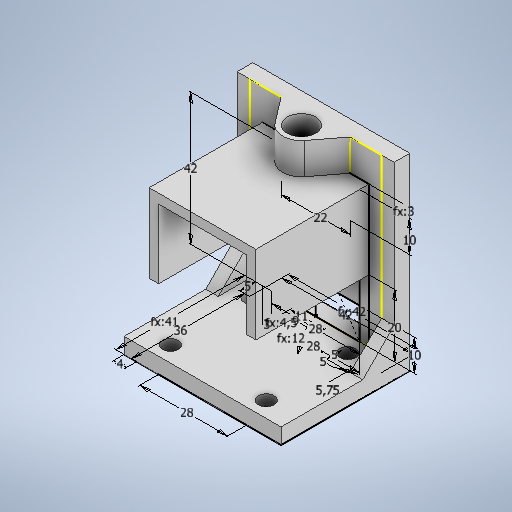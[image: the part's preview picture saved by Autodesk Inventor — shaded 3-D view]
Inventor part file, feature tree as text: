
AUTODESK INVENTOR PART (.ipt)
format: ipt  version: 2025 (Build 290162000, 162)  size: 386,560 bytes
history: native  units: mm
features: extrude x10, thread x4, sketch x2, chamfer x2, other x1, projected_geometry x1
ambient origin geometry x8: Origin, YZ Plane, XZ Plane, XY Plane, X Axis, Y Axis, Z Axis, Center Point
bodies: Body1 (feature_tree)
feature tree (20):
  other  "Bryła1"
  sketch  "Szkic1"
  extrude  "Wyciągnięcie proste1"  Depth=5.0mm
  extrude  "Wyciągnięcie proste2"  Depth=5.75mm
  extrude  "Wyciągnięcie proste3"  Depth=5.0mm
  extrude  "Wyciągnięcie proste4"  Depth=5.0mm
  sketch  "Szkic3"
  extrude  "Wyciągnięcie proste5"  Depth=42.0mm
  extrude  "Wyciągnięcie proste6"  Depth=4.5mm
  extrude  "Wyciągnięcie proste7"  Depth=12.0mm
  extrude  "Wyciągnięcie proste8"  Depth=11.0mm
  extrude  "Wyciągnięcie proste9"  Depth=5.0mm TaperAngle=0.0deg
  extrude  "Wyciągnięcie proste10"  Depth=60.0mm TaperAngle=0.0deg
  chamfer  "Faza1"  Distance=50.0mm
  chamfer  "Faza2"  Distance=5.0mm
  thread  "Gwint1"
  thread  "Gwint2"
  thread  "Gwint3"
  thread  "Gwint4"
  projected_geometry  "Pętla rzutowana1"
